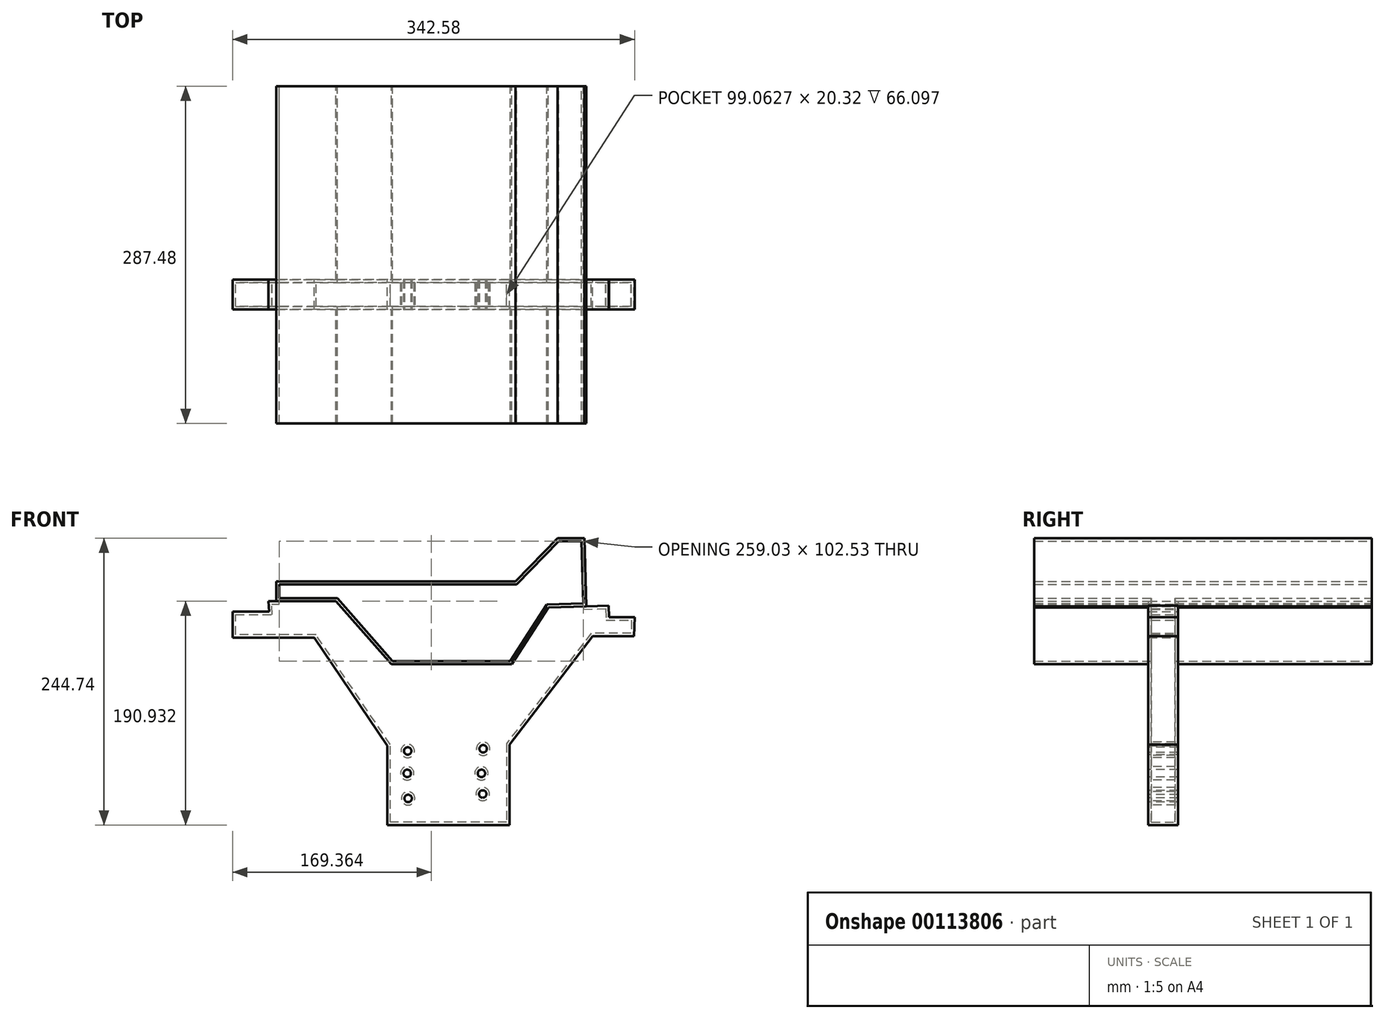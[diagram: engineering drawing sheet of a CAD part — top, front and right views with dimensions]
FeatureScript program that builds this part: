
annotation { "Feature Type Name" : "Feature", "Feature Type Description" : "" }
export const myFeature = defineFeature(function(context is Context, id is Id, definition is map)
    precondition{}
    {
        {
            var Q0;
            Q0=qCreatedBy(makeId("Front.planeOp"),FACE);
            var sketch = newSketch(context, id + "F0", { "sketchPlane" : qUnion([Q0])});
            skLineSegment(sketch, "E0", {"start": v(-112.16, 109.83) * mm, "end": v(-54.67, 109.83) * mm});
            skLineSegment(sketch, "E1", {"start": v(-54.67, 109.83) * mm, "end": v(-7.55, 56.1) * mm});
            skLineSegment(sketch, "E2", {"start": v(-7.55, 56.1) * mm, "end": v(95.18, 56.1) * mm});
            skLineSegment(sketch, "E3", {"start": v(95.18, 56.1) * mm, "end": v(126.28, 104.64) * mm});
            skLineSegment(sketch, "E4", {"start": v(126.28, 104.64) * mm, "end": v(177.64, 106.06) * mm});
            skLineSegment(sketch, "E5", {"start": v(177.64, 106.06) * mm, "end": v(177.92, 96.14) * mm});
            skLineSegment(sketch, "E6", {"start": v(177.92, 96.14) * mm, "end": v(199.8, 96.16) * mm});
            skLineSegment(sketch, "E7", {"start": v(199.8, 96.16) * mm, "end": v(199.32, 80.14) * mm});
            skLineSegment(sketch, "E8", {"start": v(199.32, 80.14) * mm, "end": v(163.98, 80.14) * mm});
            skLineSegment(sketch, "E9", {"start": v(163.98, 80.14) * mm, "end": v(93.3, -12.22) * mm});
            skLineSegment(sketch, "E10", {"start": v(93.3, -12.22) * mm, "end": v(93.3, -81.02) * mm});
            skLineSegment(sketch, "E11", {"start": v(93.3, -81.02) * mm, "end": v(-10.85, -81.02) * mm});
            skLineSegment(sketch, "E12", {"start": v(-10.85, -81.02) * mm, "end": v(-10.85, -13.16) * mm});
            skLineSegment(sketch, "E13", {"start": v(-10.85, -13.16) * mm, "end": v(-73.05, 78.73) * mm});
            skLineSegment(sketch, "E14", {"start": v(-73.05, 78.73) * mm, "end": v(-142.8, 78.73) * mm});
            skLineSegment(sketch, "E15", {"start": v(-142.8, 78.73) * mm, "end": v(-142.8, 100.87) * mm});
            skLineSegment(sketch, "E16", {"start": v(-142.8, 100.87) * mm, "end": v(-111.7, 100.87) * mm});
            skLineSegment(sketch, "E17", {"start": v(-111.7, 100.87) * mm, "end": v(-112.16, 110.3) * mm});
            skSolve(sketch);
        }
        {
            var Q0;
            {var subQ0=sQuery(id+"F0.wireOp",EDGE,"E1");Q0=makeQuery(id+"F0.imprint","IMPRINT",FACE,{"disambiguationData":[TD([[makeQuery(id+"F0.imprint","IMPRINT",EDGE,{"derivedFrom":subQ0}),-1.0]])]});}
            extrude(context, id + "F1", {"entities" : qUnion([Q0]), "depth" : 25.4 * mm});
        }
        {
            var Q0;
            Q0=makeQuery(id+"F1.opExtrude","CAP_FACE",FACE,{"disambiguationData":[OSD([sQuery(id+"F0.wireOp",EDGE,"E0"),sQuery(id+"F0.wireOp",EDGE,"E1"),sQuery(id+"F0.wireOp",EDGE,"E2"),sQuery(id+"F0.wireOp",EDGE,"E3"),sQuery(id+"F0.wireOp",EDGE,"E4"),sQuery(id+"F0.wireOp",EDGE,"E5"),sQuery(id+"F0.wireOp",EDGE,"E6"),sQuery(id+"F0.wireOp",EDGE,"E7"),sQuery(id+"F0.wireOp",EDGE,"E8"),sQuery(id+"F0.wireOp",EDGE,"E9"),sQuery(id+"F0.wireOp",EDGE,"E10"),sQuery(id+"F0.wireOp",EDGE,"E11"),sQuery(id+"F0.wireOp",EDGE,"E12"),sQuery(id+"F0.wireOp",EDGE,"E13"),sQuery(id+"F0.wireOp",EDGE,"E14"),sQuery(id+"F0.wireOp",EDGE,"E15"),sQuery(id+"F0.wireOp",EDGE,"E16"),sQuery(id+"F0.wireOp",EDGE,"E17")])],"isStart":false});
            var sketch = newSketch(context, id + "F2", { "sketchPlane" : qUnion([Q0])});
            skCircle(sketch, "E18", {"center": v(6.8, -58.14) * mm, "radius": 6.13 * mm});
            skCircle(sketch, "E19", {"center": v(6.04, -36.82) * mm, "radius": 5.32 * mm});
            skCircle(sketch, "E20", {"center": v(6.42, -17.75) * mm, "radius": 6.62 * mm});
            skCircle(sketch, "E21", {"center": v(70.75, -15.88) * mm, "radius": 7.1 * mm});
            skCircle(sketch, "E22", {"center": v(69.25, -36.82) * mm, "radius": 3.53 * mm});
            skCircle(sketch, "E23", {"center": v(70.37, -54.4) * mm, "radius": 6.7 * mm});
            skSolve(sketch);
        }
        {
            var Q0;
            Q0=sQuery(id+"F2.wireOp",VERTEX,"E21.center");
            var Q1;
            Q1=sQuery(id+"F2.wireOp",VERTEX,"E22.center");
            var Q2;
            Q2=sQuery(id+"F2.wireOp",VERTEX,"E23.center");
            var Q3;
            Q3=sQuery(id+"F2.wireOp",VERTEX,"E18.center");
            var Q4;
            Q4=sQuery(id+"F2.wireOp",VERTEX,"E19.center");
            var Q5;
            Q5=sQuery(id+"F2.wireOp",VERTEX,"E20.center");
            var Q6;
            Q6=makeQuery(id+"F1.opExtrude","SWEPT_BODY",BODY,{"disambiguationData":[OSD([sQuery(id+"F0.wireOp",EDGE,"E0"),sQuery(id+"F0.wireOp",EDGE,"E1"),sQuery(id+"F0.wireOp",EDGE,"E2"),sQuery(id+"F0.wireOp",EDGE,"E3"),sQuery(id+"F0.wireOp",EDGE,"E4"),sQuery(id+"F0.wireOp",EDGE,"E5"),sQuery(id+"F0.wireOp",EDGE,"E6"),sQuery(id+"F0.wireOp",EDGE,"E7"),sQuery(id+"F0.wireOp",EDGE,"E8"),sQuery(id+"F0.wireOp",EDGE,"E9"),sQuery(id+"F0.wireOp",EDGE,"E10"),sQuery(id+"F0.wireOp",EDGE,"E11"),sQuery(id+"F0.wireOp",EDGE,"E12"),sQuery(id+"F0.wireOp",EDGE,"E13"),sQuery(id+"F0.wireOp",EDGE,"E14"),sQuery(id+"F0.wireOp",EDGE,"E15"),sQuery(id+"F0.wireOp",EDGE,"E16"),sQuery(id+"F0.wireOp",EDGE,"E17")])]});
            hole(context, id + "F3", {"style" : HoleStyle.SIMPLE, "endStyle" : HoleEndStyle.THROUGH, "holeDiameter" : 6.35 * mm, "locations" : qUnion([Q0, Q1, Q2, Q3, Q4, Q5]), "scope" : qUnion([Q6]), "isTappedThrough" : true});
        }
        {
            var Q0;
            Q0=makeQuery(id+"F1.opExtrude","CAP_FACE",FACE,{"disambiguationData":[OSD([sQuery(id+"F0.wireOp",EDGE,"E0"),sQuery(id+"F0.wireOp",EDGE,"E1"),sQuery(id+"F0.wireOp",EDGE,"E2"),sQuery(id+"F0.wireOp",EDGE,"E3"),sQuery(id+"F0.wireOp",EDGE,"E4"),sQuery(id+"F0.wireOp",EDGE,"E5"),sQuery(id+"F0.wireOp",EDGE,"E6"),sQuery(id+"F0.wireOp",EDGE,"E7"),sQuery(id+"F0.wireOp",EDGE,"E8"),sQuery(id+"F0.wireOp",EDGE,"E9"),sQuery(id+"F0.wireOp",EDGE,"E10"),sQuery(id+"F0.wireOp",EDGE,"E11"),sQuery(id+"F0.wireOp",EDGE,"E12"),sQuery(id+"F0.wireOp",EDGE,"E13"),sQuery(id+"F0.wireOp",EDGE,"E14"),sQuery(id+"F0.wireOp",EDGE,"E15"),sQuery(id+"F0.wireOp",EDGE,"E16"),sQuery(id+"F0.wireOp",EDGE,"E17")])],"isStart":false});
            var sketch = newSketch(context, id + "F4", { "sketchPlane" : qUnion([Q0])});
            skLineSegment(sketch, "E24", {"start": v(-105.48, 109.83) * mm, "end": v(-54.67, 109.83) * mm});
            skLineSegment(sketch, "E25", {"start": v(-54.67, 109.83) * mm, "end": v(-7.55, 56.1) * mm});
            skLineSegment(sketch, "E26", {"start": v(-7.55, 56.1) * mm, "end": v(95.18, 56.1) * mm});
            skLineSegment(sketch, "E27", {"start": v(95.18, 56.1) * mm, "end": v(126.28, 104.64) * mm});
            skLineSegment(sketch, "E28", {"start": v(126.28, 104.64) * mm, "end": v(158.7, 105.54) * mm});
            skLineSegment(sketch, "E29", {"start": v(158.7, 105.54) * mm, "end": v(157.1, 163.72) * mm});
            skLineSegment(sketch, "E30", {"start": v(-105.48, 109.83) * mm, "end": v(-105.48, 126.68) * mm});
            skLineSegment(sketch, "E31", {"start": v(-105.48, 126.68) * mm, "end": v(98.32, 126.68) * mm});
            skLineSegment(sketch, "E32", {"start": v(98.32, 126.68) * mm, "end": v(134.18, 163.72) * mm});
            skLineSegment(sketch, "E33", {"start": v(134.18, 163.72) * mm, "end": v(157.1, 163.72) * mm});
            skSolve(sketch);
        }
        {
            var Q0;
            Q0=makeQuery(id+"F4.imprint","IMPRINT",FACE,{"disambiguationData":[TD([[makeQuery(id+"F4.imprint","IMPRINT",EDGE,{"derivedFrom":sQuery(id+"F4.wireOp",EDGE,"E24")}),1.0]])]});
            extrude(context, id + "F5", {"entities" : qUnion([Q0]), "operationType" : NewBodyOperationType.ADD, "depth" : 97.15 * mm, "hasSecondDirection" : true, "secondDirectionOppositeDirection" : true, "secondDirectionDepth" : 190.33 * mm});
        }
        {
            var Q0;
            Q0=makeQuery(id+"F5.opExtrude","CAP_FACE",FACE,{"disambiguationData":[OSD([sQuery(id+"F4.wireOp",EDGE,"E24"),sQuery(id+"F4.wireOp",EDGE,"E25"),sQuery(id+"F4.wireOp",EDGE,"E26"),sQuery(id+"F4.wireOp",EDGE,"E27"),sQuery(id+"F4.wireOp",EDGE,"E28"),sQuery(id+"F4.wireOp",EDGE,"E29"),sQuery(id+"F4.wireOp",EDGE,"E30"),sQuery(id+"F4.wireOp",EDGE,"E31"),sQuery(id+"F4.wireOp",EDGE,"E32"),sQuery(id+"F4.wireOp",EDGE,"E33")])],"isStart":false});
            var Q1;
            Q1=makeQuery(id+"F5.opExtrude","CAP_FACE",FACE,{"disambiguationData":[OSD([sQuery(id+"F4.wireOp",EDGE,"E24"),sQuery(id+"F4.wireOp",EDGE,"E25"),sQuery(id+"F4.wireOp",EDGE,"E26"),sQuery(id+"F4.wireOp",EDGE,"E27"),sQuery(id+"F4.wireOp",EDGE,"E28"),sQuery(id+"F4.wireOp",EDGE,"E29"),sQuery(id+"F4.wireOp",EDGE,"E30"),sQuery(id+"F4.wireOp",EDGE,"E31"),sQuery(id+"F4.wireOp",EDGE,"E32"),sQuery(id+"F4.wireOp",EDGE,"E33")])],"isStart":true});
            shell(context, id + "F6", {"entities" : qUnion([Q0, Q1]), "thickness" : 2.54 * mm});
        }
    });
